# Revit family: Gamme Turia 2V EI 30-60 - Tunnel
name_source: partatom
category: Portes
units: mm (PartAtom-declared; Revit-internal decimal feet)

## family parameters
Basée sur le plan de construction = Non
Couper avec des vides une fois chargée = Non
Partagée = Non
Repère de localisation dans la pièce = Non
Toujours verticalement = Oui

## types (8) — shared parameters
Construction analytique = <Aucun>
Définir les propriétés thermiques par = Type schématique
zero-valued in all types: Elévation par défaut, Hauteur, Largeur

## per-type parameters (varying)
| type | Côte_passage_libre_180 | Côte_passage_libre_90 | Côte_passage_libre_Hauteur | Fabricant | Hauteur Réservation | Hauteur brute | Largeur Réservation | Largeur brute | Modèle |
| Turia_2V - 1800 x 2100 | 1810 mm  [stored 5.93832 ft] | 1770 mm | 2100 mm | PORTEMETAL | 2178 mm  [stored 7.14567 ft] | 0 mm  [stored 0 ft] | 1956 mm  [stored 6.41732 ft] | 0 mm  [stored 0 ft] | NEO |
| Turia_2V - 1800 x 2400 | 1810 mm  [stored 5.93832 ft] | 1770 mm | 2400 mm |  | 2478 mm  [stored 8.12992 ft] | 0 mm  [stored 0 ft] | 1956 mm  [stored 6.41732 ft] | 0 mm  [stored 0 ft] |  |
| Neo_2V - 2000*2200 | 1854 mm  [stored 6.08268 ft] | 1814 mm | 2122 mm  [stored 6.96194 ft] | PORTEMETAL | 2200 mm | 2200 mm | 2000 mm  [stored 6.56168 ft] | 2000 mm  [stored 6.56168 ft] | NEO |
| Turia_2V - 1600-2200 | 1454 mm  [stored 4.77034 ft] | 1414 mm | 2122 mm  [stored 6.96194 ft] | PORTEMETAL | 2200 mm | 2200 mm | 1600 mm  [stored 5.24934 ft] | 1600 mm  [stored 5.24934 ft] | TURIA |
| Neo_2V - 2000 x 2201 | 2000 mm  [stored 6.56168 ft] | 1960 mm  [stored 6.43045 ft] | 2100 mm | PORTEMETAL | 2178 mm  [stored 7.14567 ft] | 2178 mm  [stored 7.14567 ft] | 2146 mm  [stored 7.04068 ft] | 2146 mm  [stored 7.04068 ft] | NEO |
| Turia_2V - 2146*2178 | 2000 mm  [stored 6.56168 ft] | 1960 mm  [stored 6.43045 ft] | 2100 mm | PORTEMETAL | 2178 mm  [stored 7.14567 ft] | 2178 mm  [stored 7.14567 ft] | 2146 mm  [stored 7.04068 ft] | 2146 mm  [stored 7.04068 ft] | TURIA |
| Neo_2V - 2146*2178 | 2000 mm  [stored 6.56168 ft] | 1960 mm  [stored 6.43045 ft] | 2100 mm | PORTEMETAL | 2178 mm  [stored 7.14567 ft] | 2178 mm  [stored 7.14567 ft] | 2146 mm  [stored 7.04068 ft] | 2146 mm  [stored 7.04068 ft] | PREMIUM NEO |
| Turia_2V - 1746*2178 | 1600 mm  [stored 5.24934 ft] | 1560 mm  [stored 5.11811 ft] | 2100 mm | PORTEMETAL | 2178 mm  [stored 7.14567 ft] | 2178 mm  [stored 7.14567 ft] | 1746 mm  [stored 5.72835 ft] | 1746 mm  [stored 5.72835 ft] | PREMIUM TURIA |

note: [stored X ft] marks values corroborated as IEEE doubles in the binary element streams (Revit-internal decimal feet)
